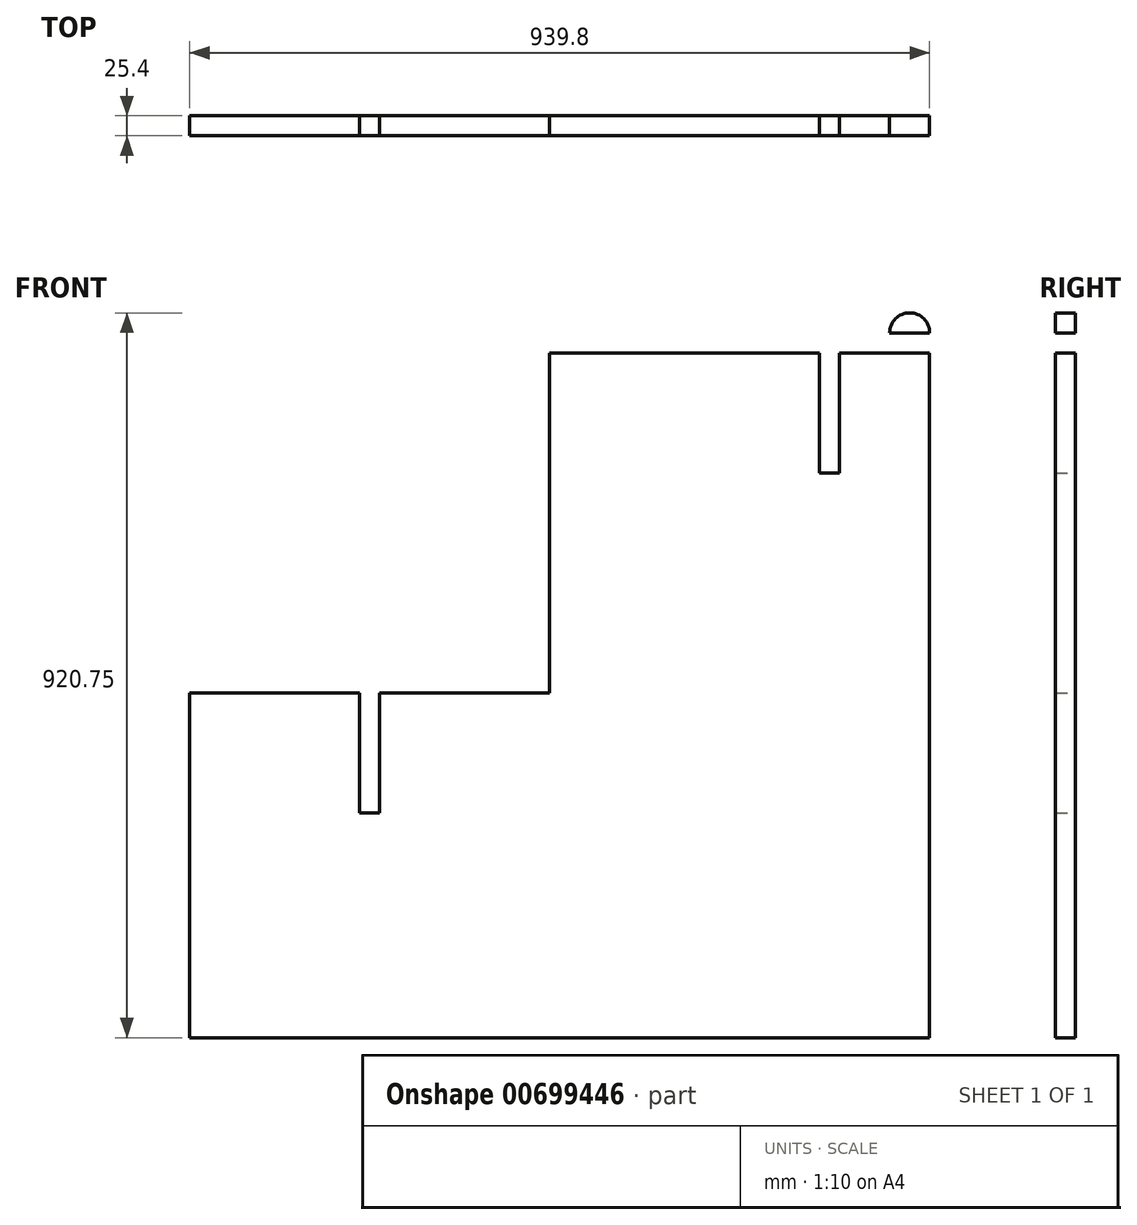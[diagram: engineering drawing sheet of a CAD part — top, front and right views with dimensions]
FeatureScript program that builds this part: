
annotation { "Feature Type Name" : "Feature", "Feature Type Description" : "" }
export const myFeature = defineFeature(function(context is Context, id is Id, definition is map)
    precondition{}
    {
        {
            var Q0;
            Q0=qCreatedBy(makeId("Front.planeOp"),FACE);
            var sketch = newSketch(context, id + "F0", { "sketchPlane" : qUnion([Q0])});
            skLineSegment(sketch, "E0", {"start": v(0, 0) * mm, "end": v(939.8, 0) * mm});
            skLineSegment(sketch, "E1", {"start": v(939.8, 0) * mm, "end": v(939.8, 869.95) * mm});
            skLineSegment(sketch, "E2", {"start": v(939.8, 869.95) * mm, "end": v(457.2, 869.95) * mm});
            skLineSegment(sketch, "E3", {"start": v(457.2, 869.95) * mm, "end": v(457.2, 438.15) * mm});
            skLineSegment(sketch, "E4", {"start": v(457.2, 438.15) * mm, "end": v(0, 438.15) * mm});
            skLineSegment(sketch, "E5", {"start": v(0, 438.15) * mm, "end": v(0, 0) * mm});
            skLineSegment(sketch, "E6.bottom", {"start": v(825.5, 869.95) * mm, "end": v(800.1, 869.95) * mm});
            skLineSegment(sketch, "E6.top", {"start": v(825.5, 717.55) * mm, "end": v(800.1, 717.55) * mm});
            skLineSegment(sketch, "E6.left", {"start": v(825.5, 869.95) * mm, "end": v(825.5, 717.55) * mm});
            skLineSegment(sketch, "E6.right", {"start": v(800.1, 869.95) * mm, "end": v(800.1, 717.55) * mm});
            skLineSegment(sketch, "E7.bottom", {"start": v(215.9, 438.15) * mm, "end": v(241.3, 438.15) * mm});
            skLineSegment(sketch, "E7.top", {"start": v(215.9, 285.75) * mm, "end": v(241.3, 285.75) * mm});
            skLineSegment(sketch, "E7.left", {"start": v(215.9, 438.15) * mm, "end": v(215.9, 285.75) * mm});
            skLineSegment(sketch, "E7.right", {"start": v(241.3, 438.15) * mm, "end": v(241.3, 285.75) * mm});
            skLineSegment(sketch, "E8.bottom", {"start": v(939.8, 869.95) * mm, "end": v(914.4, 869.95) * mm});
            skLineSegment(sketch, "E8.top", {"start": v(939.8, 895.35) * mm, "end": v(914.4, 895.35) * mm});
            skLineSegment(sketch, "E8.left", {"start": v(939.8, 869.95) * mm, "end": v(939.8, 895.35) * mm});
            skLineSegment(sketch, "E8.right", {"start": v(914.4, 869.95) * mm, "end": v(914.4, 895.35) * mm});
            skArc(sketch, "E9", {"start": v(939.8, 895.35) * mm, "mid": v(914.4, 920.75) * mm, "end": v(889, 895.35) * mm});
            skLineSegment(sketch, "E10", {"start": v(914.4, 895.35) * mm, "end": v(889, 895.35) * mm});
            skSolve(sketch);
        }
        {
            var Q0;
            Q0=makeQuery(id+"F0.imprint","IMPRINT",FACE,{"disambiguationData":[TD([[makeQuery(id+"F0.imprint","IMPRINT",EDGE,{"derivedFrom":sQuery(id+"F0.wireOp",EDGE,"E8.top")}),-1.0]])]});
            var Q1;
            Q1=makeQuery(id+"F0.imprint","IMPRINT",FACE,{"disambiguationData":[TD([[makeQuery(id+"F0.imprint","IMPRINT",EDGE,{"derivedFrom":sQuery(id+"F0.wireOp",EDGE,"E8.bottom")}),-1.0]])]});
            var Q2;
            Q2=makeQuery(id+"F0.imprint","IMPRINT",FACE,{"disambiguationData":[TD([[makeQuery(id+"F0.imprint","IMPRINT",EDGE,{"derivedFrom":sQuery(id+"F0.wireOp",EDGE,"E0")}),1.0]])]});
            extrude(context, id + "F1", {"entities" : qUnion([Q0, Q1, Q2]), "depth" : 25.4 * mm, "offsetDistance" : 25.4 * mm, "symmetric" : true});
        }
    });
